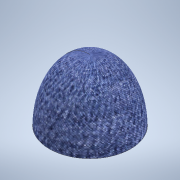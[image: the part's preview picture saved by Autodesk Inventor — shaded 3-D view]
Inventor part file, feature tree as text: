
AUTODESK INVENTOR PART (.ipt)
format: ipt  version: 2022 (Build 260153000, 153)  size: 269,312 bytes
history: native  units: in
note: dims shown in document units (in); Inventor stores cm internally (conversion verified against a paired STEP export)
features: sketch x2, revolve x1, shell x1
ambient origin geometry x8: Origin, YZ Plane, XZ Plane, XY Plane, X Axis, Y Axis, Z Axis, Center Point
bodies: Solid1 (feature_tree)
feature tree (4):
  revolve  "Revolution1"  [1 undecoded]
  shell  "Shell1"  Thickness=90.0deg
  sketch  "Sketch12"  dims[d3=0.25in d40=0.5in d41=0.0344in d42=0.5in d43=0.0344in]
  sketch  "Sketch1"  dims[d0=1.45in d1=2.45in d2=90.0deg]
note: 1 required parameter value undecoded (feature->parameter linkage not recoverable at this tier; creation-order binding heuristic only, values carry confidence <= 0.55)
